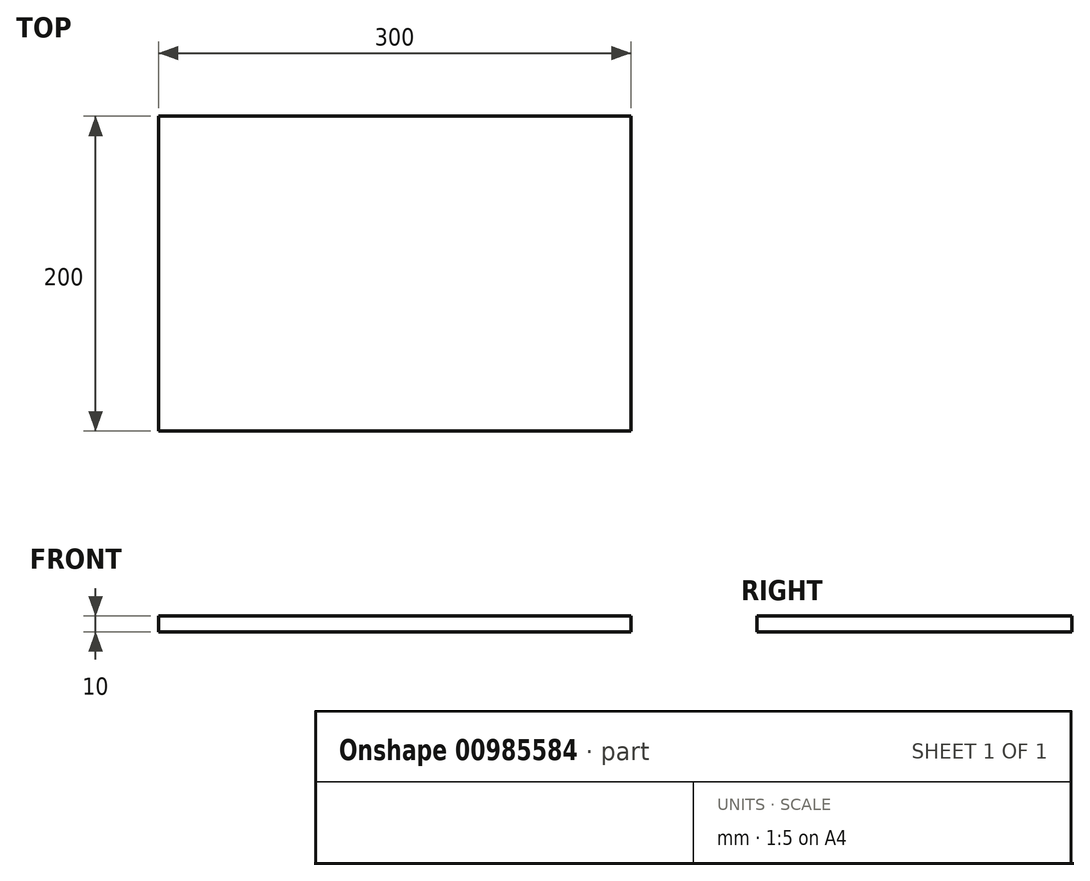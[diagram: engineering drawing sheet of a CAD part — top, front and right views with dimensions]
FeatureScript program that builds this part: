
annotation { "Feature Type Name" : "Feature", "Feature Type Description" : "" }
export const myFeature = defineFeature(function(context is Context, id is Id, definition is map)
    precondition{}
    {
        {
            var Q0;
            Q0=qCreatedBy(makeId("Top.planeOp"),FACE);
            var sketch = newSketch(context, id + "F0", { "sketchPlane" : qUnion([Q0])});
            skLineSegment(sketch, "E0.bottom", {"start": v(150, 100) * mm, "end": v(-150, 100) * mm});
            skLineSegment(sketch, "E0.top", {"start": v(150, -100) * mm, "end": v(-150, -100) * mm});
            skLineSegment(sketch, "E0.left", {"start": v(150, 100) * mm, "end": v(150, -100) * mm});
            skLineSegment(sketch, "E0.right", {"start": v(-150, 100) * mm, "end": v(-150, -100) * mm});
            skPoint(sketch, "E0.middle", {"position": v(0, 0) * mm});
            skSolve(sketch);
        }
        {
            var Q0;
            Q0=makeQuery(id+"F0.imprint","IMPRINT",FACE,{"disambiguationData":[TD([[makeQuery(id+"F0.imprint","IMPRINT",EDGE,{"derivedFrom":sQuery(id+"F0.wireOp",EDGE,"E0.bottom")}),1.0]])]});
            extrude(context, id + "F1", {"entities" : qUnion([Q0]), "depth" : 10 * mm, "offsetDistance" : 25 * mm});
        }
    });
